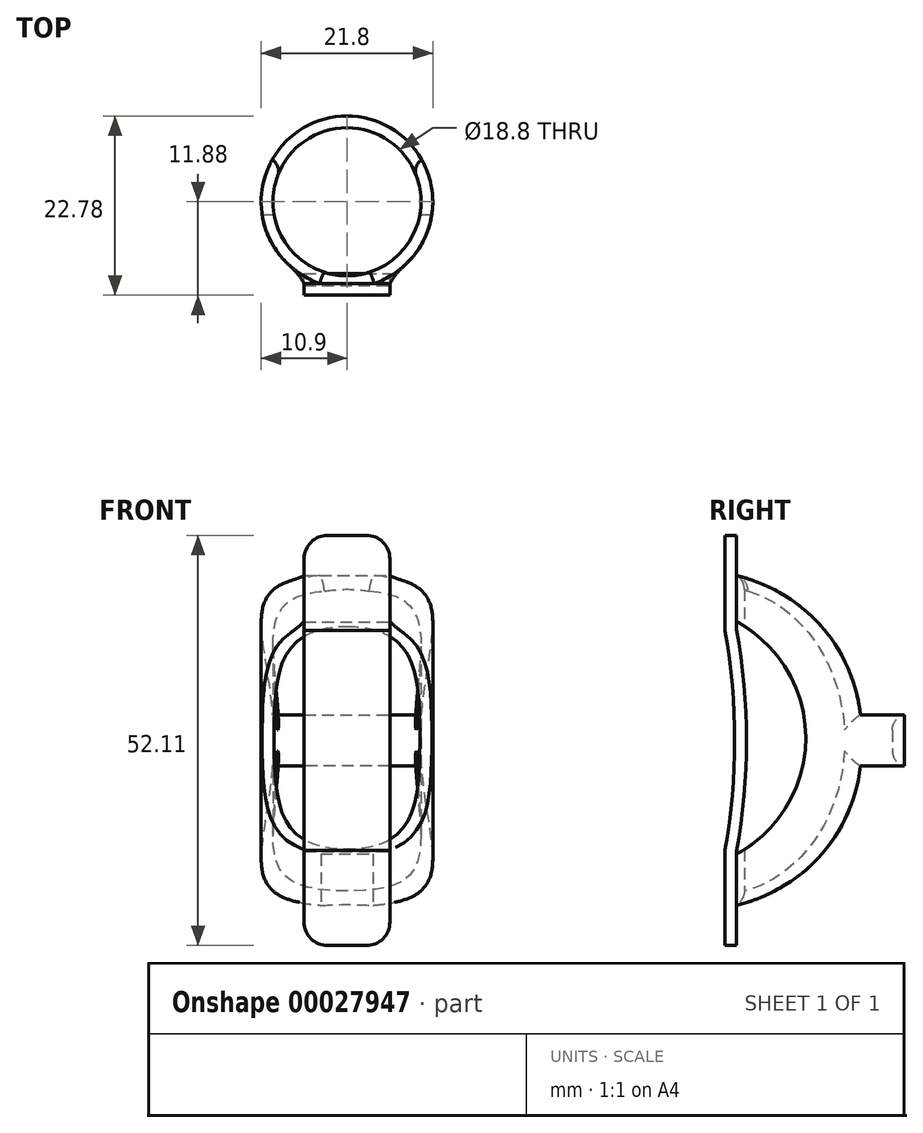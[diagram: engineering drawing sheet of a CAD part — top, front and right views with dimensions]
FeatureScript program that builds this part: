
annotation { "Feature Type Name" : "Feature", "Feature Type Description" : "" }
export const myFeature = defineFeature(function(context is Context, id is Id, definition is map)
    precondition{}
    {
        {
            assignVariable(context, id + "F0", {"name" : "fingerDiam", "anyValue" : 18.8});
        }
        {
            assignVariable(context, id + "F1", {"name" : "length", "anyValue" : getVariable(context, 'fingerDiam') * 2.24});
        }
        {
            assignVariable(context, id + "F2", {"name" : "outerDiam", "anyValue" : getVariable(context, 'fingerDiam') + 3});
        }
        {
            var Q0;
            Q0=qCreatedBy(makeId("Top.planeOp"),FACE);
            var sketch = newSketch(context, id + "F3", { "sketchPlane" : qUnion([Q0])});
            skCircle(sketch, "E0", {"center": v(0, 0) * mm, "radius": 9.4 * mm});
            skCircle(sketch, "E1", {"center": v(0, 0) * mm, "radius": 10.9 * mm});
            skSolve(sketch);
        }
        {
            var Q0;
            Q0=makeQuery(id+"F3.imprint","IMPRINT",FACE,{"disambiguationData":[TD([[makeQuery(id+"F3.imprint","IMPRINT",EDGE,{"derivedFrom":sQuery(id+"F3.wireOp",EDGE,"E0")}),-1.0]])]});
            extrude(context, id + "F4", {"entities" : qUnion([Q0]), "depth" : (getVariable(context, 'length')) * mm});
        }
        {
            var Q0;
            Q0=qCreatedBy(makeId("Right.planeOp"),FACE);
            cPlane(context, id + "F5", {"entities" : qUnion([Q0]), "cplaneType" : CPlaneType.OFFSET, "offset" : (getVariable(context, 'outerDiam') / 2) * mm, "width" : 150 * mm, "height" : 150 * mm});
        }
        {
            var Q0;
            Q0=qCreatedBy(id+"F5.planeOp",FACE);
            var sketch = newSketch(context, id + "F6", { "sketchPlane" : qUnion([Q0])});
            skLineSegment(sketch, "E2.0", {"start": v(-10.9, 42.11) * mm, "end": v(10.9, 42.11) * mm});
            skLineSegment(sketch, "E3.0", {"start": v(-10.9, 0) * mm, "end": v(10.9, 0) * mm});
            skLineSegment(sketch, "E4", {"start": v(-10.9, 0) * mm, "end": v(-10.9, 42.75) * mm});
            skLineSegment(sketch, "E5", {"start": v(-11.9, 36.86) * mm, "end": v(-11.9, 5.9) * mm});
            skLineSegment(sketch, "E6", {"start": v(-10.9, 21.38) * mm, "end": v(6.32, 21.38) * mm, "construction": true});
            skPoint(sketch, "E6.endSnap0", {"position": v(-10.9, 21.38) * mm});
            skArc(sketch, "E7", {"start": v(-11.9, 5.9) * mm, "mid": v(-1.6, 21.38) * mm, "end": v(-11.9, 36.86) * mm});
            skLineSegment(sketch, "E8", {"start": v(0, 42.11) * mm, "end": v(0, 12.16) * mm, "construction": true});
            skPoint(sketch, "E8.endSnap0", {"position": v(0, 42.11) * mm});
            skSolve(sketch);
        }
        {
            var Q0;
            {var subQ0=sQuery(id+"F6.wireOp",EDGE,"E7");var subQ1=sQuery(id+"F6.wireOp",EDGE,"E4");var subQ2=makeQuery(id+"F6.imprint","INTERSECT",VERTEX,{"disambiguationData":[OD(0.0)],"derivedFrom":[subQ1,subQ0]});Q0=makeQuery(id+"F6.imprint","IMPRINT",FACE,{"disambiguationData":[TD([[makeQuery(id+"F6.imprint","IMPRINT",EDGE,{"disambiguationData":[TD([[subQ2,-1.0]])],"derivedFrom":subQ1}),-1.0]])]});}
            extrude(context, id + "F7", {"entities" : qUnion([Q0]), "operationType" : NewBodyOperationType.REMOVE, "endBound" : BoundingType.THROUGH_ALL, "oppositeDirection" : true, "depth" : 25 * mm});
        }
        {
            var Q0;
            Q0=qCreatedBy(id+"F5.planeOp",FACE);
            var sketch = newSketch(context, id + "F8", { "sketchPlane" : qUnion([Q0])});
            skLineSegment(sketch, "E9", {"start": v(10.9, 21.06) * mm, "end": v(-15.49, 21.06) * mm, "construction": true});
            skPoint(sketch, "E9.endSnap0", {"position": v(10.9, 21.06) * mm});
            skLineSegment(sketch, "E10.0", {"start": v(-10.9, 42.11) * mm, "end": v(22.2, 42.11) * mm});
            skLineSegment(sketch, "E11.0", {"start": v(-10.9, 0) * mm, "end": v(22.2, 0) * mm});
            skArc(sketch, "E12", {"start": v(-10.9, 0) * mm, "mid": v(0.22, 6.3) * mm, "end": v(5.82, 17.8) * mm});
            skPoint(sketch, "E13.orphan", {"position": v(10.9, 41.74) * mm});
            skPoint(sketch, "E14.end.orphan", {"position": v(10.9, 0.38) * mm});
            skLineSegment(sketch, "E15", {"start": v(5.82, 24.3) * mm, "end": v(16.31, 24.3) * mm});
            skLineSegment(sketch, "E16", {"start": v(16.31, 24.3) * mm, "end": v(16.31, 17.8) * mm});
            skLineSegment(sketch, "E17", {"start": v(16.31, 17.8) * mm, "end": v(5.82, 17.8) * mm});
            skLineSegment(sketch, "E18.right", {"start": v(22.2, 42.11) * mm, "end": v(22.2, 0) * mm});
            skArc(sketch, "E19.trimOffspring", {"start": v(5.82, 24.3) * mm, "mid": v(0.22, 35.8) * mm, "end": v(-10.9, 42.11) * mm});
            skPoint(sketch, "E20.orphan", {"position": v(10.9, 42.11) * mm});
            skPoint(sketch, "E21.orphan", {"position": v(10.9, 0) * mm});
            skSolve(sketch);
        }
        {
            var Q0;
            Q0=makeQuery(id+"F8.imprint","IMPRINT",FACE,{"disambiguationData":[TD([[makeQuery(id+"F8.imprint","IMPRINT",EDGE,{"derivedFrom":sQuery(id+"F8.wireOp",EDGE,"E10.0")}),-1.0]])]});
            extrude(context, id + "F9", {"entities" : qUnion([Q0]), "operationType" : NewBodyOperationType.REMOVE, "oppositeDirection" : true, "depth" : 25 * mm});
        }
        {
            var Q0;
            Q0=qCreatedBy(makeId("Top.planeOp"),FACE);
            cPlane(context, id + "F10", {"entities" : qUnion([Q0]), "cplaneType" : CPlaneType.OFFSET, "offset" : 5 * mm, "oppositeDirection" : true, "width" : 150 * mm, "height" : 150 * mm});
        }
        {
            var Q0;
            Q0=qCreatedBy(id+"F10.planeOp",FACE);
            var sketch = newSketch(context, id + "F11", { "sketchPlane" : qUnion([Q0])});
            skLineSegment(sketch, "E22.bottom", {"start": v(-5.45, -11.88) * mm, "end": v(5.45, -11.88) * mm});
            skLineSegment(sketch, "E22.top", {"start": v(-5.45, -10.38) * mm, "end": v(5.45, -10.38) * mm});
            skLineSegment(sketch, "E22.left", {"start": v(-5.45, -11.88) * mm, "end": v(-5.45, -10.38) * mm});
            skLineSegment(sketch, "E22.right", {"start": v(5.45, -11.88) * mm, "end": v(5.45, -10.38) * mm});
            skLineSegment(sketch, "E23", {"start": v(0, 0) * mm, "end": v(0, -17.12) * mm, "construction": true});
            skSolve(sketch);
        }
        {
            var Q0;
            Q0=qCreatedBy(makeId("Right.planeOp"),FACE);
            var sketch = newSketch(context, id + "F12", { "sketchPlane" : qUnion([Q0])});
            skLineSegment(sketch, "E24", {"start": v(-10.93, 42.11) * mm, "end": v(-10.93, 35.11) * mm});
            skLineSegment(sketch, "E25", {"start": v(9.9, 21.06) * mm, "end": v(-13.48, 21.06) * mm, "construction": true});
            skLineSegment(sketch, "E26.MirrorCS", {"start": v(-10.93, 0) * mm, "end": v(-10.93, 7) * mm});
            skArc(sketch, "E27", {"start": v(-10.93, 7) * mm, "mid": v(-9.68, 21.06) * mm, "end": v(-10.93, 35.11) * mm});
            skLineSegment(sketch, "E28", {"start": v(-10.93, 42.11) * mm, "end": v(-10.93, 47.11) * mm});
            skLineSegment(sketch, "E29.MirrorCS", {"start": v(-10.93, 0) * mm, "end": v(-10.93, -5) * mm});
            skLineSegment(sketch, "E30.0", {"start": v(10.9, 24.3) * mm, "end": v(5.82, 24.3) * mm, "construction": true});
            skLineSegment(sketch, "E31.0", {"start": v(5.82, 17.8) * mm, "end": v(10.9, 17.8) * mm, "construction": true});
            skLineSegment(sketch, "E32", {"start": v(-10.93, 35.11) * mm, "end": v(-10.93, 7) * mm, "construction": true});
            skPoint(sketch, "E33", {"position": v(-9.68, 21.06) * mm});
            skSolve(sketch);
        }
        {
            var Q0;
            Q0=makeQuery(id+"F11.imprint","IMPRINT",FACE,{"disambiguationData":[TD([[makeQuery(id+"F11.imprint","IMPRINT",EDGE,{"derivedFrom":sQuery(id+"F11.wireOp",EDGE,"E22.bottom")}),1.0]])]});
            var Q1;
            Q1=sQuery(id+"F11.wireOp",EDGE,"E22.top");
            var Q2;
            Q2=sQuery(id+"F11.wireOp",EDGE,"E22.right");
            var Q3;
            Q3=sQuery(id+"F11.wireOp",EDGE,"E22.bottom");
            var Q4;
            Q4=sQuery(id+"F11.wireOp",EDGE,"E22.left");
            var Q5;
            Q5=sQuery(id+"F12.wireOp",EDGE,"E29.MirrorCS");
            var Q6;
            Q6=sQuery(id+"F12.wireOp",EDGE,"E26.MirrorCS");
            var Q7;
            Q7=sQuery(id+"F12.wireOp",EDGE,"E27");
            var Q8;
            Q8=sQuery(id+"F12.wireOp",EDGE,"E24");
            var Q9;
            Q9=sQuery(id+"F12.wireOp",EDGE,"E28");
            sweep(context, id + "F13", {"operationType" : NewBodyOperationType.ADD, "profiles" : qUnion([Q0]), "surfaceProfiles" : qUnion([Q1, Q2, Q3, Q4]), "path" : qUnion([Q5, Q6, Q7, Q8, Q9])});
        }
        {
            var Q0;
            Q0=makeQuery(id+"F13.opSweep","CAP_EDGE",EDGE,{"disambiguationData":[OSD([sQuery(id+"F11.wireOp",EDGE,"E22.right"),sQuery(id+"F12.wireOp",VERTEX,"E29.MirrorCS.end")])],"isStart":true});
            var Q1;
            Q1=makeQuery(id+"F13.opSweep","CAP_EDGE",EDGE,{"disambiguationData":[OSD([sQuery(id+"F11.wireOp",EDGE,"E22.left"),sQuery(id+"F12.wireOp",VERTEX,"E29.MirrorCS.end")])],"isStart":true});
            var Q2;
            Q2=makeQuery(id+"F13.opSweep","CAP_EDGE",EDGE,{"disambiguationData":[OSD([sQuery(id+"F11.wireOp",EDGE,"E22.left"),sQuery(id+"F12.wireOp",VERTEX,"E28.end")])],"isStart":false});
            var Q3;
            Q3=makeQuery(id+"F13.opSweep","CAP_EDGE",EDGE,{"disambiguationData":[OSD([sQuery(id+"F11.wireOp",EDGE,"E22.right"),sQuery(id+"F12.wireOp",VERTEX,"E28.end")])],"isStart":false});
            fillet(context, id + "F14", {"entities" : qUnion([Q0, Q1, Q2, Q3]), "radius" : 3 * mm, "tangentPropagation" : true, "allowEdgeOverflow" : false});
        }
        {
            var Q0;
            Q0=makeQuery(id+"F13.boolean.opBoolean","INTERSECT",EDGE,{"disambiguationData":[OD(1.0)],"derivedFrom":[makeQuery(id+"F4.opExtrude","SWEPT_FACE",FACE,{"disambiguationData":[OSD([sQuery(id+"F3.wireOp",EDGE,"E1")])]}),makeQuery(id+"F13.opSweep","SWEPT_FACE",FACE,{"disambiguationData":[OSD([sQuery(id+"F11.wireOp",EDGE,"E22.top"),sQuery(id+"F12.wireOp",EDGE,"E28")])]})]});
            var Q1;
            Q1=makeQuery(id+"F13.boolean.opBoolean","INTERSECT",EDGE,{"disambiguationData":[OD(1.0)],"derivedFrom":[makeQuery(id+"F4.opExtrude","SWEPT_FACE",FACE,{"disambiguationData":[OSD([sQuery(id+"F3.wireOp",EDGE,"E1")])]}),makeQuery(id+"F13.opSweep","SWEPT_FACE",FACE,{"disambiguationData":[OSD([sQuery(id+"F11.wireOp",EDGE,"E22.top"),sQuery(id+"F12.wireOp",EDGE,"E26.MirrorCS")])]})]});
            var Q2;
            Q2=makeQuery(id+"F13.boolean.opBoolean","INTERSECT",EDGE,{"disambiguationData":[OD(0.0)],"derivedFrom":[makeQuery(id+"F4.opExtrude","SWEPT_FACE",FACE,{"disambiguationData":[OSD([sQuery(id+"F3.wireOp",EDGE,"E1")])]}),makeQuery(id+"F13.opSweep","SWEPT_FACE",FACE,{"disambiguationData":[OSD([sQuery(id+"F11.wireOp",EDGE,"E22.top"),sQuery(id+"F12.wireOp",EDGE,"E28")])]})]});
            var Q3;
            Q3=makeQuery(id+"F13.boolean.opBoolean","INTERSECT",EDGE,{"disambiguationData":[OD(0.0)],"derivedFrom":[makeQuery(id+"F4.opExtrude","SWEPT_FACE",FACE,{"disambiguationData":[OSD([sQuery(id+"F3.wireOp",EDGE,"E1")])]}),makeQuery(id+"F13.opSweep","SWEPT_FACE",FACE,{"disambiguationData":[OSD([sQuery(id+"F11.wireOp",EDGE,"E22.top"),sQuery(id+"F12.wireOp",EDGE,"E26.MirrorCS")])]})]});
            fillet(context, id + "F15", {"entities" : qUnion([Q0, Q1, Q2, Q3]), "radius" : 8 * mm, "tangentPropagation" : true, "allowEdgeOverflow" : false});
        }
        {
            var Q0;
            Q0=makeQuery(id+"F9.boolean.opBoolean","INTERSECT",EDGE,{"derivedFrom":[makeQuery(id+"F4.opExtrude","SWEPT_FACE",FACE,{"disambiguationData":[OSD([sQuery(id+"F3.wireOp",EDGE,"E0")])]}),makeQuery(id+"F9.opExtrude","SWEPT_FACE",FACE,{"disambiguationData":[OSD([sQuery(id+"F8.wireOp",EDGE,"E19.trimOffspring")])]})]});
            var Q1;
            Q1=makeQuery(id+"F9.boolean.opBoolean","INTERSECT",EDGE,{"derivedFrom":[makeQuery(id+"F4.opExtrude","SWEPT_FACE",FACE,{"disambiguationData":[OSD([sQuery(id+"F3.wireOp",EDGE,"E0")])]}),makeQuery(id+"F9.opExtrude","SWEPT_FACE",FACE,{"disambiguationData":[OSD([sQuery(id+"F8.wireOp",EDGE,"E12")])]})]});
            var Q2;
            Q2=makeQuery(id+"F9.boolean.opBoolean","INTERSECT",EDGE,{"derivedFrom":[makeQuery(id+"F4.opExtrude","SWEPT_FACE",FACE,{"disambiguationData":[OSD([sQuery(id+"F3.wireOp",EDGE,"E0")])]}),makeQuery(id+"F9.opExtrude","SWEPT_FACE",FACE,{"disambiguationData":[OSD([sQuery(id+"F8.wireOp",EDGE,"E17")])]})]});
            var Q3;
            Q3=makeQuery(id+"F9.boolean.opBoolean","INTERSECT",EDGE,{"derivedFrom":[makeQuery(id+"F4.opExtrude","SWEPT_FACE",FACE,{"disambiguationData":[OSD([sQuery(id+"F3.wireOp",EDGE,"E0")])]}),makeQuery(id+"F9.opExtrude","SWEPT_FACE",FACE,{"disambiguationData":[OSD([sQuery(id+"F8.wireOp",EDGE,"E15")])]})]});
            fillet(context, id + "F16", {"entities" : qUnion([Q0, Q1, Q2, Q3]), "radius" : 2 * mm, "tangentPropagation" : true, "allowEdgeOverflow" : false});
        }
    });
